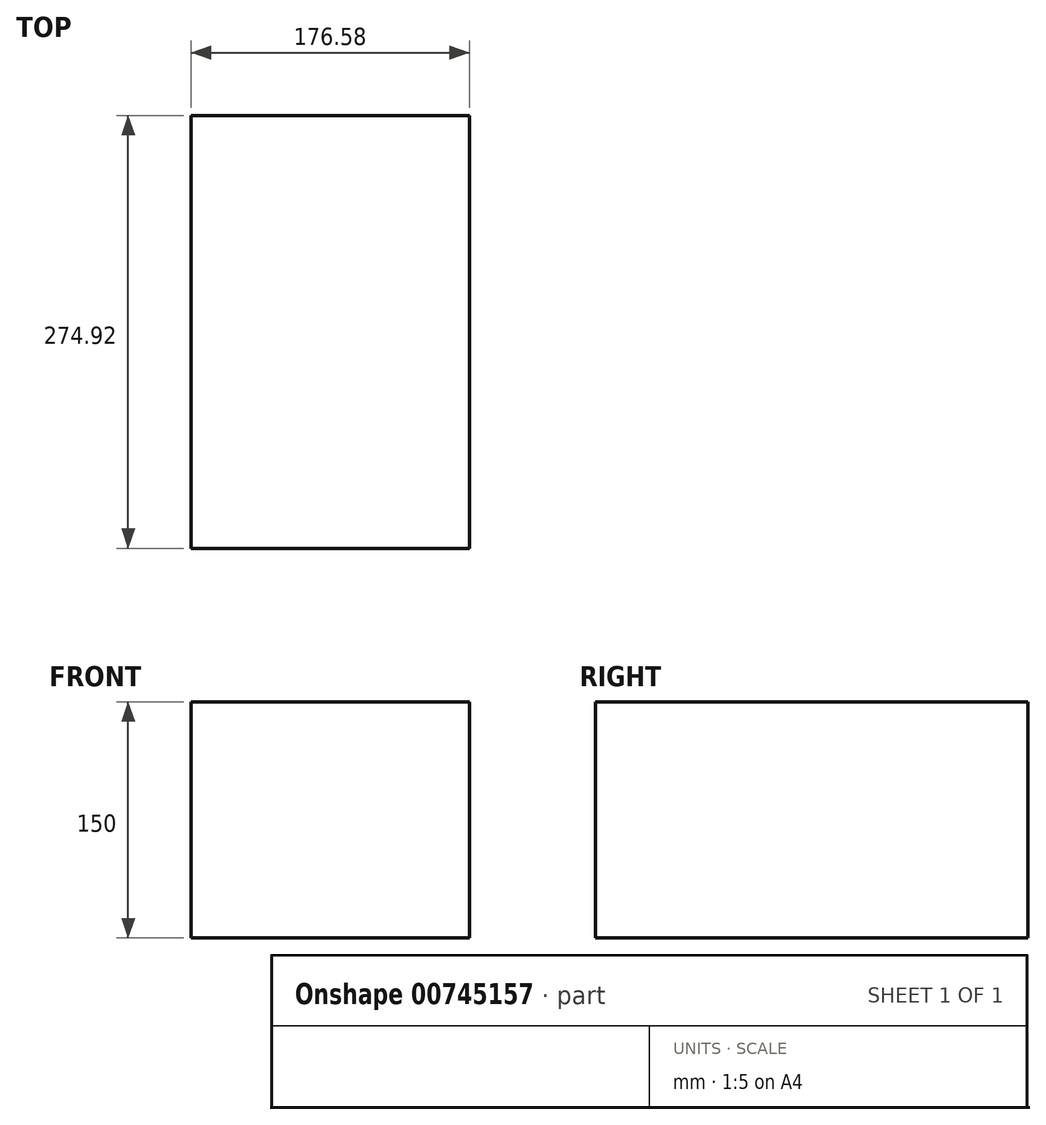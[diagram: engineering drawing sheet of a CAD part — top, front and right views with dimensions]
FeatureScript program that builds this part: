
annotation { "Feature Type Name" : "Feature", "Feature Type Description" : "" }
export const myFeature = defineFeature(function(context is Context, id is Id, definition is map)
    precondition{}
    {
        {
            var Q0;
            Q0=qCreatedBy(makeId("Top.planeOp"),FACE);
            var sketch = newSketch(context, id + "F0", { "sketchPlane" : qUnion([Q0])});
            skLineSegment(sketch, "E0.bottom", {"start": v(-94.16, 157.3) * mm, "end": v(82.42, 157.3) * mm});
            skLineSegment(sketch, "E0.top", {"start": v(-94.16, -117.63) * mm, "end": v(82.42, -117.63) * mm});
            skLineSegment(sketch, "E0.left", {"start": v(-94.16, 157.3) * mm, "end": v(-94.16, -117.63) * mm});
            skLineSegment(sketch, "E0.right", {"start": v(82.42, 157.3) * mm, "end": v(82.42, -117.63) * mm});
            skSolve(sketch);
        }
        {
            var Q0;
            Q0=makeQuery(id+"F0.imprint","IMPRINT",FACE,{"disambiguationData":[TD([[makeQuery(id+"F0.imprint","IMPRINT",EDGE,{"derivedFrom":sQuery(id+"F0.wireOp",EDGE,"E0.bottom")}),-1.0]])]});
            extrude(context, id + "F1", {"entities" : qUnion([Q0]), "depth" : 150 * mm, "offsetDistance" : 25 * mm});
        }
    });
